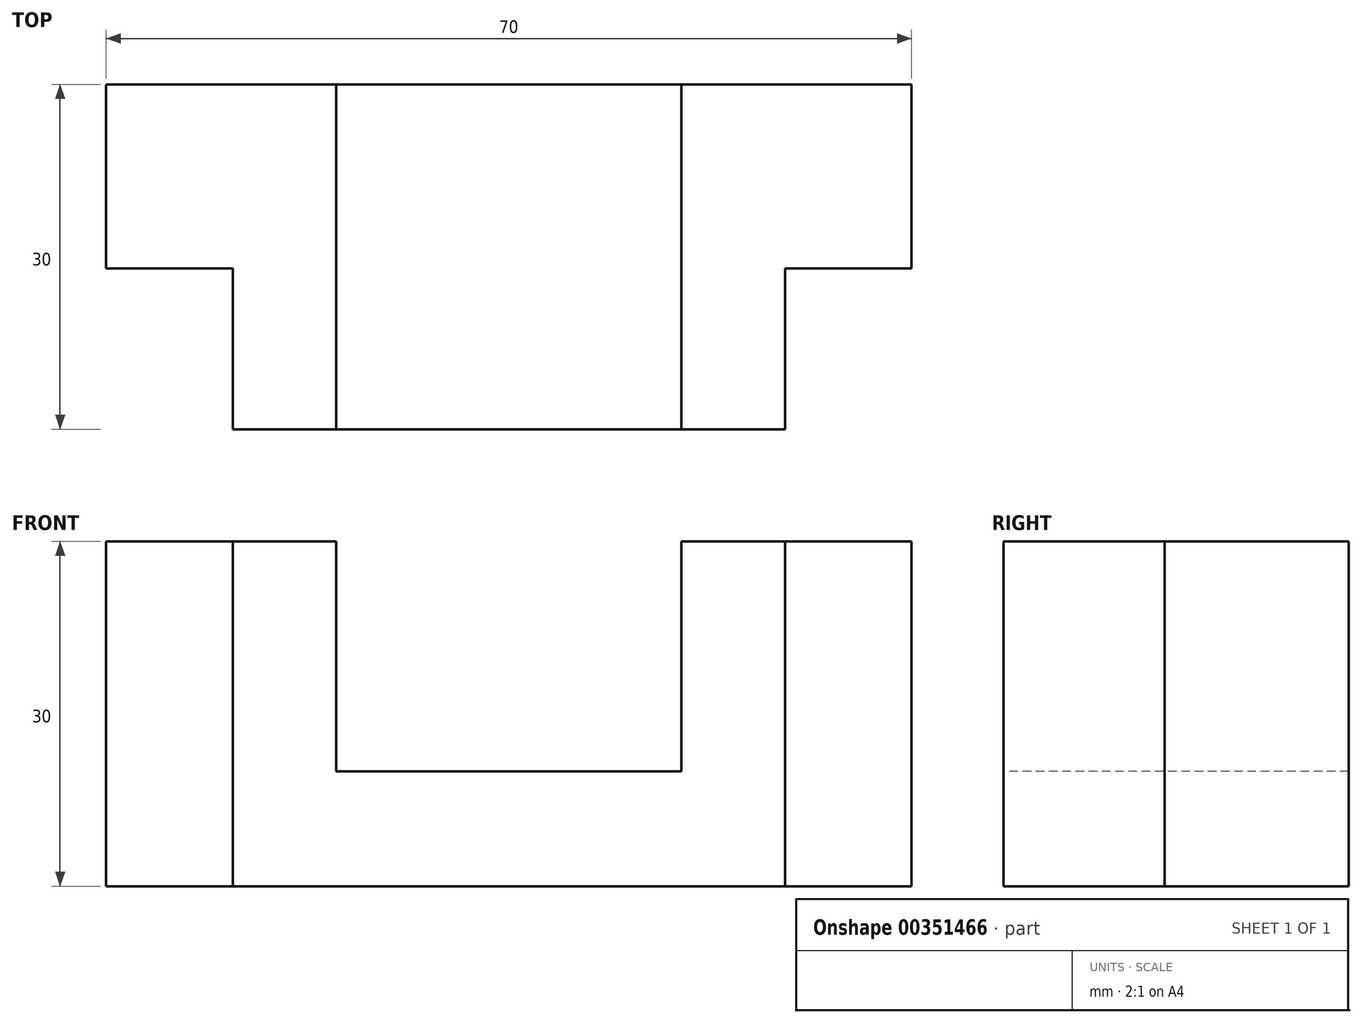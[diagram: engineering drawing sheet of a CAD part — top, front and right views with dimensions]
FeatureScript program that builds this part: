
annotation { "Feature Type Name" : "Feature", "Feature Type Description" : "" }
export const myFeature = defineFeature(function(context is Context, id is Id, definition is map)
    precondition{}
    {
        {
            var Q0;
            Q0=qCreatedBy(makeId("Top.planeOp"),FACE);
            var sketch = newSketch(context, id + "F0", { "sketchPlane" : qUnion([Q0])});
            skLineSegment(sketch, "E0", {"start": v(0, 0) * mm, "end": v(0, 14) * mm});
            skLineSegment(sketch, "E1", {"start": v(0, 14) * mm, "end": v(-11, 14) * mm});
            skLineSegment(sketch, "E2", {"start": v(-11, 14) * mm, "end": v(-11, 30) * mm});
            skLineSegment(sketch, "E3", {"start": v(59, 30) * mm, "end": v(59, 14) * mm});
            skLineSegment(sketch, "E4", {"start": v(59, 14) * mm, "end": v(48, 14) * mm});
            skLineSegment(sketch, "E5", {"start": v(48, 14) * mm, "end": v(48, 0) * mm});
            skLineSegment(sketch, "E6", {"start": v(48, 0) * mm, "end": v(0, 0) * mm});
            skLineSegment(sketch, "E7", {"start": v(59, 30) * mm, "end": v(-11, 30) * mm});
            skSolve(sketch);
        }
        {
            var Q0;
            Q0=makeQuery(id+"F0.imprint","IMPRINT",FACE,{"disambiguationData":[TD([[makeQuery(id+"F0.imprint","IMPRINT",EDGE,{"derivedFrom":sQuery(id+"F0.wireOp",EDGE,"E0")}),-1.0]])]});
            extrude(context, id + "F1", {"entities" : qUnion([Q0]), "depth" : 30 * mm});
        }
        {
            var Q0;
            Q0=makeQuery(id+"F1.opExtrude","SWEPT_FACE",FACE,{"disambiguationData":[OSD([sQuery(id+"F0.wireOp",EDGE,"E6")])]});
            var sketch = newSketch(context, id + "F2", { "sketchPlane" : qUnion([Q0])});
            skLineSegment(sketch, "E8.bottom", {"start": v(9, 43.56) * mm, "end": v(39, 43.56) * mm});
            skLineSegment(sketch, "E8.top", {"start": v(9, 10) * mm, "end": v(39, 10) * mm});
            skLineSegment(sketch, "E8.left", {"start": v(9, 43.56) * mm, "end": v(9, 10) * mm});
            skLineSegment(sketch, "E8.right", {"start": v(39, 43.56) * mm, "end": v(39, 10) * mm});
            skSolve(sketch);
        }
        {
            var Q0;
            {var subQ0=sQuery(id+"F2.wireOp",EDGE,"E8.top");Q0=makeQuery(id+"F2.imprint","IMPRINT",FACE,{"disambiguationData":[TD([[makeQuery(id+"F2.imprint","IMPRINT",EDGE,{"derivedFrom":subQ0}),1.0]])]});}
            extrude(context, id + "F3", {"entities" : qUnion([Q0]), "operationType" : NewBodyOperationType.REMOVE, "oppositeDirection" : true, "depth" : 40 * mm});
        }
    });
